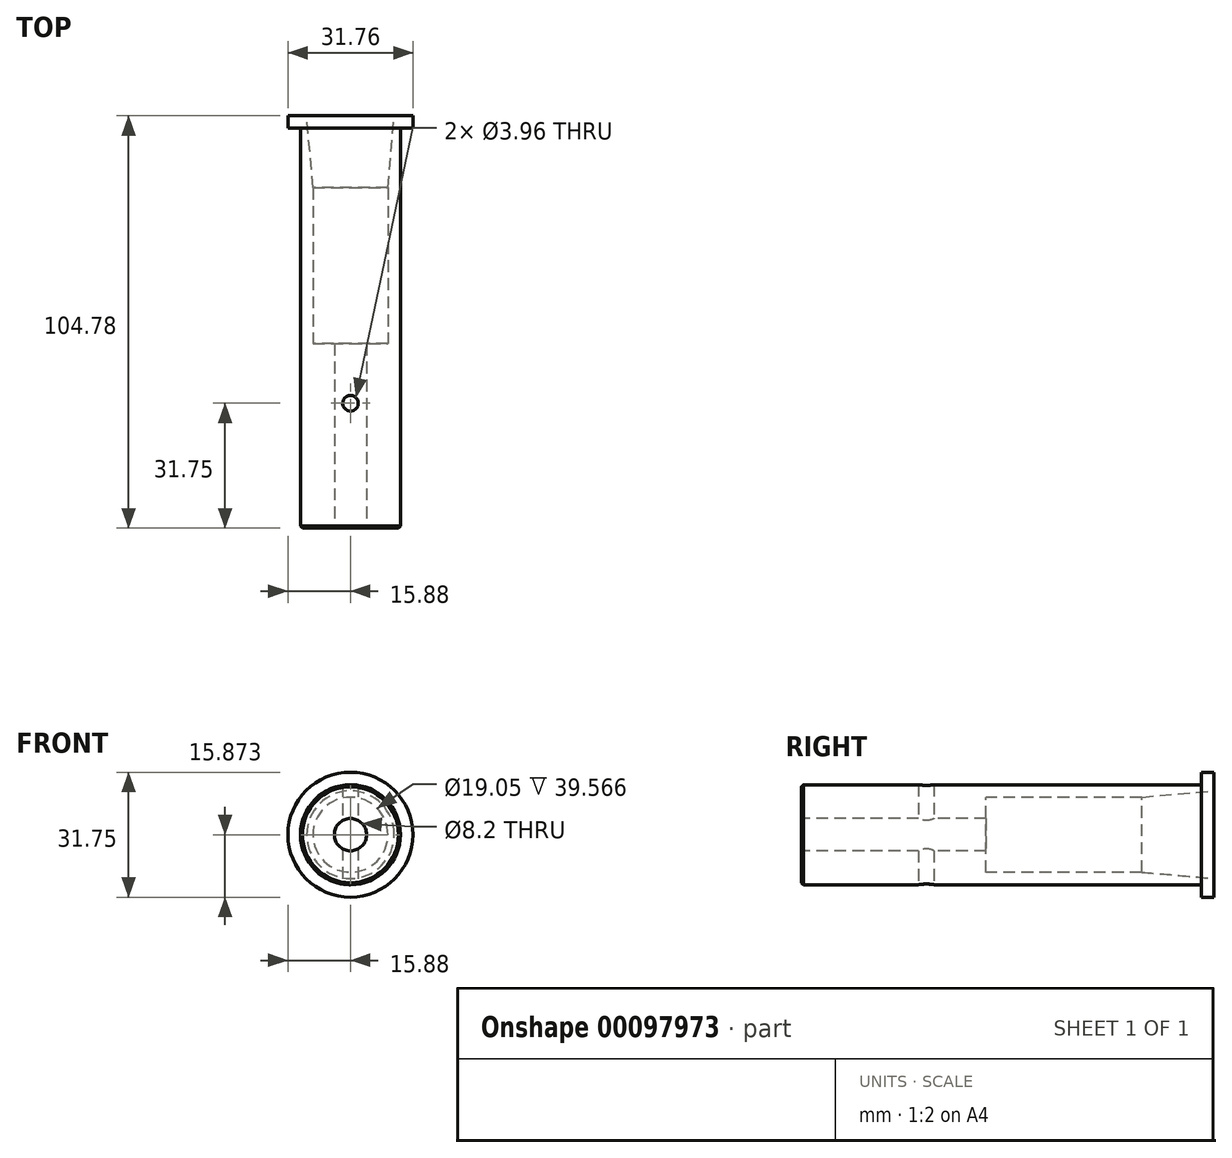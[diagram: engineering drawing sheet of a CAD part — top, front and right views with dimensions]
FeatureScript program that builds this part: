
annotation { "Feature Type Name" : "Feature", "Feature Type Description" : "" }
export const myFeature = defineFeature(function(context is Context, id is Id, definition is map)
    precondition{}
    {
        {
            var Q0;
            Q0=qCreatedBy(makeId("Right.planeOp"),FACE);
            var sketch = newSketch(context, id + "F0", { "sketchPlane" : qUnion([Q0])});
            skLineSegment(sketch, "E0.bottom", {"start": v(-101.6, 11.18) * mm, "end": v(0, 11.18) * mm});
            skLineSegment(sketch, "E0.left", {"start": v(-101.6, 11.18) * mm, "end": v(-101.6, -1.52) * mm});
            skLineSegment(sketch, "E1", {"start": v(0, 11.18) * mm, "end": v(0, 14.36) * mm});
            skLineSegment(sketch, "E2", {"start": v(0, 14.36) * mm, "end": v(3.17, 14.36) * mm});
            skLineSegment(sketch, "E3", {"start": v(3.17, 14.36) * mm, "end": v(3.17, 8) * mm});
            skLineSegment(sketch, "E4", {"start": v(-54.68, 11.18) * mm, "end": v(-54.68, -14.22) * mm, "construction": true});
            skLineSegment(sketch, "E5", {"start": v(-101.6, 8) * mm, "end": v(3.17, 8) * mm, "construction": true});
            skLineSegment(sketch, "E6", {"start": v(-101.6, -11.04) * mm, "end": v(3.17, -11.04) * mm, "construction": true});
            skLineSegment(sketch, "E7", {"start": v(-54.68, 9.6) * mm, "end": v(3.17, 9.6) * mm, "construction": true});
            skLineSegment(sketch, "E8", {"start": v(-54.68, -12.64) * mm, "end": v(3.17, -12.64) * mm, "construction": true});
            skLineSegment(sketch, "E9", {"start": v(3.18, 9.6) * mm, "end": v(-15.12, 8) * mm, "construction": true});
            skLineSegment(sketch, "E10", {"start": v(3.17, -12.64) * mm, "end": v(-15.12, -11.04) * mm, "construction": true});
            skLineSegment(sketch, "E11", {"start": v(-101.6, -1.52) * mm, "end": v(-54.68, -1.52) * mm});
            skLineSegment(sketch, "E12", {"start": v(-15.12, 8) * mm, "end": v(3.18, 9.6) * mm});
            skLineSegment(sketch, "E13", {"start": v(-54.68, 8) * mm, "end": v(-15.12, 8) * mm});
            skLineSegment(sketch, "E14", {"start": v(-54.68, 8) * mm, "end": v(-54.68, -1.52) * mm});
            skPoint(sketch, "E15.orphan", {"position": v(3.17, -1.52) * mm});
            skPoint(sketch, "E16.trimOffspring.end.orphan", {"position": v(-101.6, -14.22) * mm});
            skPoint(sketch, "E17.start.orphan", {"position": v(3.17, -17.4) * mm});
            skPoint(sketch, "E18.end.orphan", {"position": v(0, -14.22) * mm});
            skSolve(sketch);
        }
        {
            var Q0;
            Q0=makeQuery(id+"F0.imprint","IMPRINT",FACE,{"disambiguationData":[TD([[makeQuery(id+"F0.imprint","IMPRINT",EDGE,{"derivedFrom":sQuery(id+"F0.wireOp",EDGE,"E0.bottom")}),-1.0]])]});
            var Q1;
            Q1=sQuery(id+"F0.wireOp",EDGE,"E11");
            revolve(context, id + "F1", {"entities" : qUnion([Q0]), "axis" : qUnion([Q1]), "revolveType" : RevolveType.FULL});
        }
        {
            var Q0;
            Q0=makeQuery(id+"F1.opRevolve","SWEPT_FACE",FACE,{"disambiguationData":[OSD([sQuery(id+"F0.wireOp",EDGE,"E0.left")])]});
            var sketch = newSketch(context, id + "F2", { "sketchPlane" : qUnion([Q0])});
            skCircle(sketch, "E19.0.0", {"center": v(0, -1.52) * mm, "radius": 12.7 * mm, "construction": true});
            skSolve(sketch);
        }
        {
            var Q0;
            Q0=sQuery(id+"F2.wireOp",VERTEX,"E19.0.0.center");
            var Q1;
            Q1=makeQuery(id+"F1.opRevolve","SWEPT_BODY",BODY,{"disambiguationData":[OSD([sQuery(id+"F0.wireOp",EDGE,"E0.bottom"),sQuery(id+"F0.wireOp",EDGE,"E0.left"),sQuery(id+"F0.wireOp",EDGE,"E1"),sQuery(id+"F0.wireOp",EDGE,"E2"),sQuery(id+"F0.wireOp",EDGE,"E3"),sQuery(id+"F0.wireOp",EDGE,"E11"),sQuery(id+"F0.wireOp",EDGE,"E12"),sQuery(id+"F0.wireOp",EDGE,"E13"),sQuery(id+"F0.wireOp",EDGE,"E14")])]});
            hole(context, id + "F3", {"style" : HoleStyle.SIMPLE, "endStyle" : HoleEndStyle.THROUGH, "standardTappedOrClearance" : lookupTablePath({ "standard" : "ANSI", "fit" : "Close", "size" : "5/16", "type" : "Clearance" }), "standardBlindInLast" : lookupTablePath({ "fit" : "Close", "standard" : "ANSI", "size" : "5/16", "type" : "Clearance" }), "holeDiameter" : 8.2 * mm, "locations" : qUnion([Q0]), "scope" : qUnion([Q1]), "isTappedThrough" : true});
        }
        {
            var Q0;
            Q0=sQuery(id+"F2.wireOp",EDGE,"E19.0.0");
            cPlane(context, id + "F4", {"entities" : qUnion([Q0]), "cplaneType" : CPlaneType.LINE_ANGLE, "offset" : 0 * mm, "angle" : 0 * degree, "width" : 152.4 * mm, "height" : 152.4 * mm});
        }
        {
            var Q0;
            Q0=qCreatedBy(id+"F4.planeOp",FACE);
            var sketch = newSketch(context, id + "F5", { "sketchPlane" : qUnion([Q0])});
            skLineSegment(sketch, "E20.0", {"start": v(-12.7, 101.6) * mm, "end": v(12.7, 101.6) * mm, "construction": true});
            skLineSegment(sketch, "E21", {"start": v(0, 101.6) * mm, "end": v(0, 69.85) * mm, "construction": true});
            skCircle(sketch, "E22", {"center": v(0, 69.85) * mm, "radius": 1.98 * mm});
            skSolve(sketch);
        }
        {
            var Q0;
            Q0 = qSketchRegion(id + "F5", true);
            extrude(context, id + "F6", {"entities" : qUnion([Q0]), "operationType" : NewBodyOperationType.REMOVE, "endBound" : BoundingType.THROUGH_ALL, "oppositeDirection" : true, "depth" : 25.4 * mm, "hasSecondDirection" : true, "secondDirectionBound" : BoundingType.THROUGH_ALL, "secondDirectionOppositeDirection" : false, "secondDirectionDepth" : 25.4 * mm});
        }
        {
            var Q0;
            Q0=makeQuery(id+"F1.opRevolve","SWEPT_EDGE",EDGE,{"disambiguationData":[OSD([sQuery(id+"F0.wireOp",EDGE,"E0.bottom"),sQuery(id+"F0.wireOp",EDGE,"E0.left")])]});
            chamfer(context, id + "F7", {"entities" : qUnion([Q0]), "width" : 0.5 * mm, "tangentPropagation" : true});
        }
    });
